# Revit family: IS_StradaII_T3601_BIM_FR
name_source: partatom
category: Plumbing Fixtures
revit_build: Autodesk Revit 2017 (Build: 20160225_1515(x64)
units: mm (PartAtom-declared; Revit-internal decimal feet)

## family parameters
Always vertical = No
Cut with Voids When Loaded = No
OmniClass Number = 23.45.05.21.11.11
OmniClass Title = Water Operated Water Closets
Part Type = Normal
Room Calculation Point = No
Round Connector Dimension = Use Diameter
Shared = No
Work Plane-Based = No

## types (1)
- T360101 - STRADA II  SEAT & CVR WHITE THIN  SCL
    Accessoires = www.idealstandard.be
    Auteur = Ideal Standard
    BOSUseNativeGeometries = 1
    Bim-NomDuProjet = ISI_IdealStandard__STRADA_T360101
    Caractéristiques = STRADA II  SEAT & CVR WHITE THIN  SCL
    CodeBarre = 8014140448860
    ConseilsDInstallation = www.idealstandard.be
    Cost = 0 $
    Couleur = Blanc
    CouleurWc = Blanc
    CoûtDeRemplacement = 0
    DateDeCréation = 2018_08_15
    Description = STRADA II  SEAT & CVR WHITE THIN  SCL
    Dimensions = 57 x 364 x 447mm
    Espace = Interne
    Finition = Blanc
    Forme = Complexe
    Hauteur = 57 mm
    IfcExportAs = WCSEATS
    IfcExportType = IfcSanitaryTerminalType
    InformationsProduit = www.idealstandard.be
    Largeur = 364 mm
    LienUtile = www.idealstandard.be
    Longueur = 447 mm
    Manufacturer = www.idealstandard.be
    Marque = Ideal Standard
    Matériel = Plastic
    Model = T360101
    Profondeur = 0 mm  [stored 0 ft]
    Raccordement = Plomberie
    Révision = 1
    TypeDeCuvette = Washdown
    TypeDeWc = Domestic
    URL = www.idealstandard.be
    Uniclass2015Version = Products v1.1
    UnitéDeMesure = Millimètres
    UnitéDeTemps = An
    UnitéMonétaire = €
    UrlDuFabricant = www.idealstandard.be
    Version = 1

note: [stored X ft] marks values corroborated as IEEE doubles in the binary element streams (Revit-internal decimal feet)

## geometry (parser evidence)
native form markers: Sweep x2
no freeform markers — native parametric forms only
